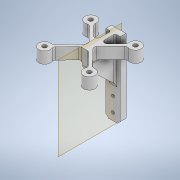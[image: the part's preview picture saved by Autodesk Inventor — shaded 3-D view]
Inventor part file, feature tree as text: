
AUTODESK INVENTOR PART (.ipt)
format: ipt  version: 2020 (Build 240168000, 168)  size: 483,840 bytes
history: native  units: mm
features: projected_geometry x15, extrude x10, sketch x10, fillet x6, thicken_offset x5, other x3, plane x1, chamfer x1, reference x1
ambient origin geometry x8: Origin, YZ Plane, XZ Plane, XY Plane, X Axis, Y Axis, Z Axis, Center Point
bodies: Solid1 (feature_tree)
feature tree (52):
  extrude  "Extrusion1"  Depth=10.0mm
  extrude  "Extrusion2"  Depth=2.0mm
  plane  "Work Plane1"
  extrude  "Extrusion3"  Depth=10.0mm
  extrude  "Extrusion4"  Depth=3.0mm
  extrude  "Extrusion5"  Depth=40.0mm
  extrude  "Extrusion6"  Depth=3.0mm
  extrude  "Extrusion7"  Depth=3.0mm TaperAngle=0.0deg
  extrude  "Extrusion8"  Depth=32.0mm
  chamfer  "Chamfer1"  Distance=3.0mm
  extrude  "Extrusion9"  Depth=3.0mm
  fillet  "Fillet3"  Radius=3.0mm
  fillet  "Fillet4"  Radius=8.0mm
  fillet  "Fillet5"  Radius=8.0mm
  thicken_offset  "Thicken1"
  extrude  "Extrusion14"  Depth=8.0mm
  thicken_offset  "Thicken2"
  thicken_offset  "Thicken3"
  thicken_offset  "Thicken4"
  thicken_offset  "Thicken5"
  fillet  "Fillet14"  Radius=8.0mm
  fillet  "Fillet15"  Radius=5.0mm
  fillet  "Fillet16"  Radius=3.0mm
  sketch  "Sketch1"  dims[d0=10.0mm d1=20.0mm]
  reference  "Reference1"
  sketch  "Sketch2"  dims[d2=2.0mm d3=2.0mm]
  projected_geometry  "Projected Loop1"
  sketch  "Sketch3"  dims[d4=10.0mm d5=30.0mm]
  projected_geometry  "Projected Loop2"
  projected_geometry  "Projected Loop3"
  sketch  "Sketch4"  dims[d6=3.0mm d7=0.0mm d8=20.0mm]
  projected_geometry  "Projected Loop4"
  sketch  "Sketch5"  dims[d9=40.0mm d10=40.0mm]
  projected_geometry  "Projected Loop5"
  sketch  "Sketch6"  dims[d11=3.0mm d12=0.0mm d13=30.0mm]
  projected_geometry  "Projected Loop6"
  sketch  "Sketch7"  dims[d14=28.0mm d15=3.0mm d16=0.0mm]
  projected_geometry  "Projected Loop7"
  projected_geometry  "Projected Loop8"
  projected_geometry  "Projected Loop9"
  projected_geometry  "Projected Loop10"
  projected_geometry  "Projected Loop11"
  sketch  "Sketch8"  dims[d17=31.0mm d18=32.0mm]
  projected_geometry  "Projected Loop12"
  sketch  "Sketch9"  dims[d19=3.0mm]
  projected_geometry  "Projected Loop13"
  sketch  "Sketch14"  dims[d20=3.0mm d21=3.0mm d22=3.0mm d23=3.0mm d24=0.0mm d25=8.0mm d26=8.0mm d27=8.0mm d28=8.0mm d29=5.0mm d30=0.0mm d31=3.0mm d32=3.0mm d33=5.0mm d34=0.0mm d35=5.0mm d36=0.0mm d37=20.0mm d38=0.0mm d39=2.0mm d40=2.0mm d41=45.0deg d42=20.0mm d43=0.0mm d46=3.0mm d47=1.0mm d48=3.0mm d55=1.0mm d56=1.0mm d78=8.0mm d79=8.0mm d80=10.0mm d81=0.0mm d82=1.0mm d83=1.0mm d84=1.0mm d85=1.0mm d86=1.0mm d87=1.0mm d88=1.0mm d89=1.0mm d90=2.0mm d91=2.0mm d92=2.0mm]
  projected_geometry  "Projected Loop21"
  projected_geometry  "Projected Loop22"
  parser-record x1  (decoder bookkeeping rows leaked as tree rows — omitted from the tree; the rows remain in map.json)
  other  "leg_1.iam"
  other  "leg_holder_2:1"
note: 1 file-system path scrubbed to <path> (originals preserved in map.json)
